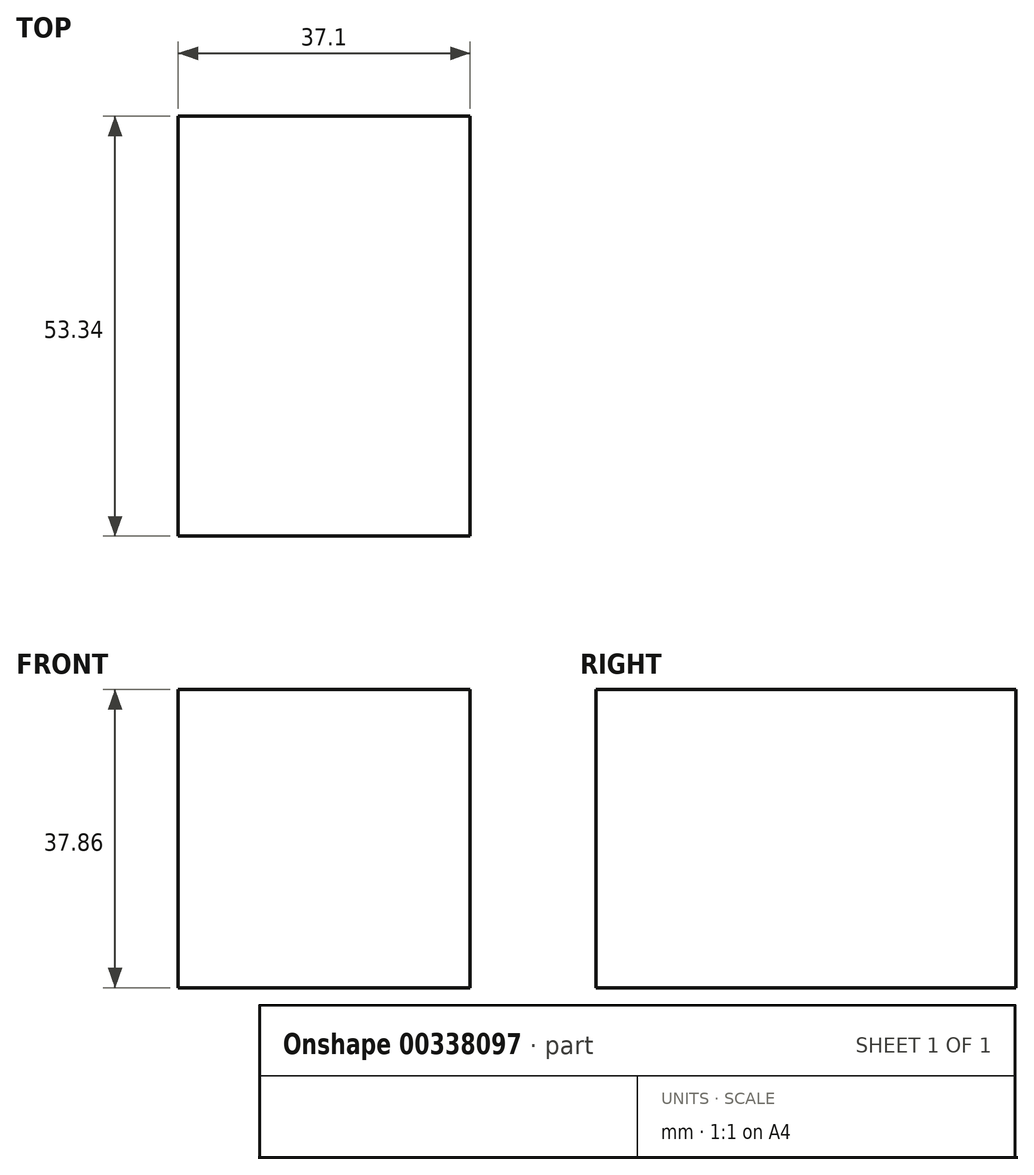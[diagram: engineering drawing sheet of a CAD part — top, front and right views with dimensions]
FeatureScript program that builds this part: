
annotation { "Feature Type Name" : "Feature", "Feature Type Description" : "" }
export const myFeature = defineFeature(function(context is Context, id is Id, definition is map)
    precondition{}
    {
        {
            var Q0;
            Q0=qCreatedBy(makeId("Front.planeOp"),FACE);
            var sketch = newSketch(context, id + "F0", { "sketchPlane" : qUnion([Q0])});
            skLineSegment(sketch, "E0.bottom", {"start": v(0, 0) * mm, "end": v(-37.1, 0) * mm});
            skLineSegment(sketch, "E0.top", {"start": v(0, 37.86) * mm, "end": v(-37.1, 37.86) * mm});
            skLineSegment(sketch, "E0.left", {"start": v(0, 0) * mm, "end": v(0, 37.86) * mm});
            skLineSegment(sketch, "E0.right", {"start": v(-37.1, 0) * mm, "end": v(-37.1, 37.86) * mm});
            skSolve(sketch);
        }
        {
            var Q0;
            Q0=makeQuery(id+"F0.imprint","IMPRINT",FACE,{"disambiguationData":[TD([[makeQuery(id+"F0.imprint","IMPRINT",EDGE,{"derivedFrom":sQuery(id+"F0.wireOp",EDGE,"E0.bottom")}),-1.0]])]});
            extrude(context, id + "F1", {"entities" : qUnion([Q0]), "depth" : 53.34 * mm});
        }
    });
